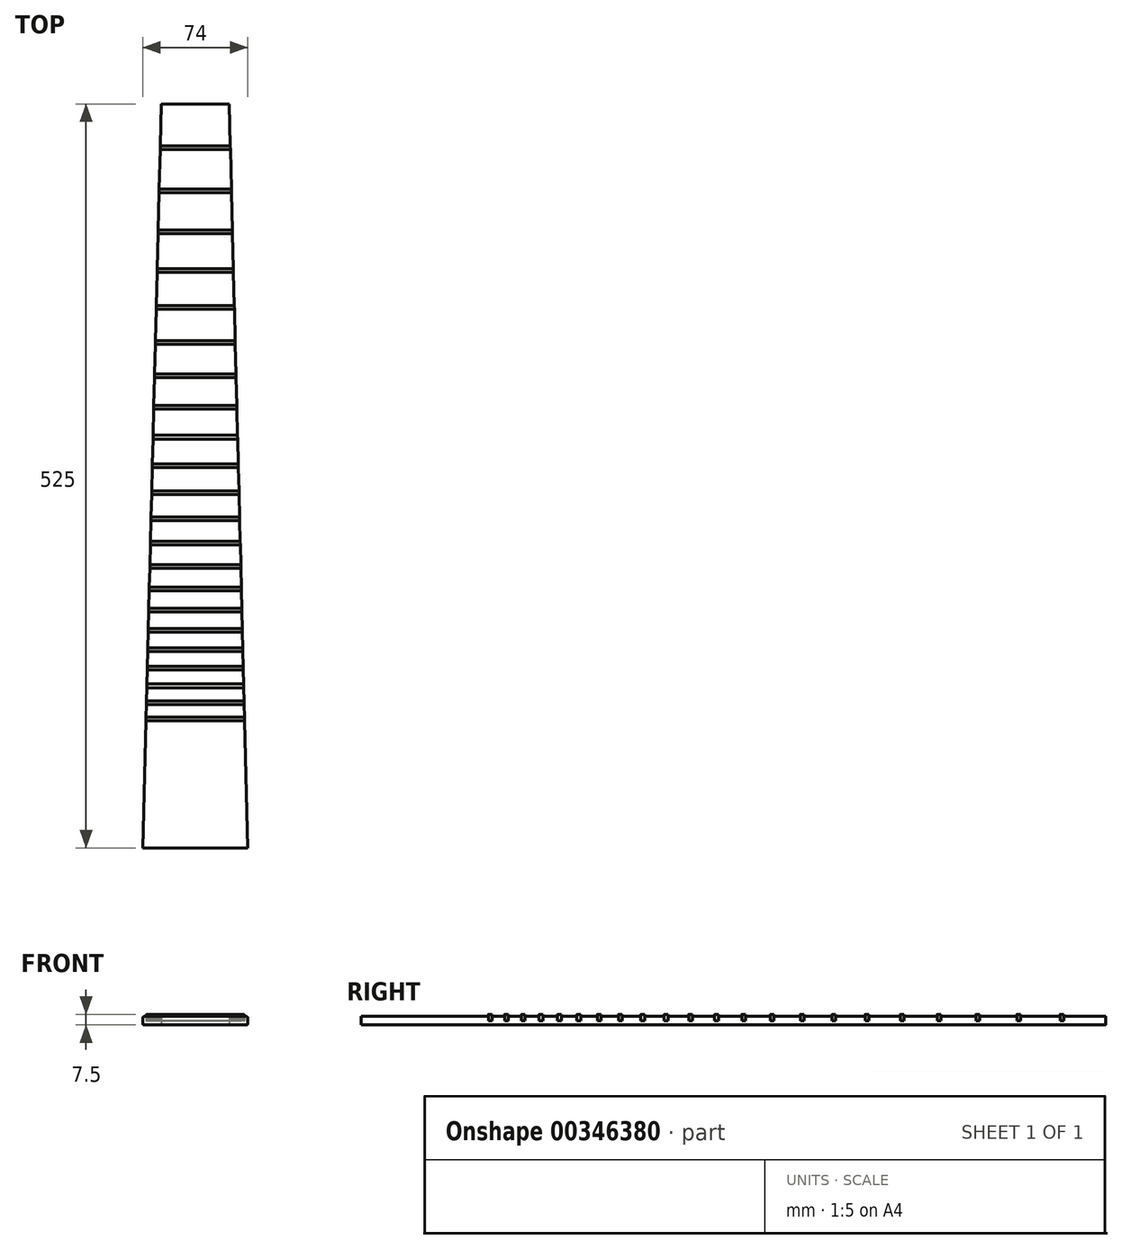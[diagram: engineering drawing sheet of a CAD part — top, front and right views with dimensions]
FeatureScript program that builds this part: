
annotation { "Feature Type Name" : "Feature", "Feature Type Description" : "" }
export const myFeature = defineFeature(function(context is Context, id is Id, definition is map)
    precondition{}
    {
        {
            var Q0;
            Q0=qCreatedBy(makeId("Top.planeOp"),FACE);
            var sketch = newSketch(context, id + "F0", { "sketchPlane" : qUnion([Q0])});
            skLineSegment(sketch, "E0", {"start": v(0, 0) * mm, "end": v(0, 525) * mm, "construction": true});
            skLineSegment(sketch, "E1", {"start": v(0, 525) * mm, "end": v(-24, 525) * mm});
            skLineSegment(sketch, "E2", {"start": v(0, 0) * mm, "end": v(-37, 0) * mm});
            skLineSegment(sketch, "E3", {"start": v(-37, 0) * mm, "end": v(-24, 525) * mm});
            skLineSegment(sketch, "E4", {"start": v(-24.73, 495.53) * mm, "end": v(0, 495.53) * mm});
            skLineSegment(sketch, "E5", {"start": v(-24.8, 492.92) * mm, "end": v(0, 492.92) * mm});
            skLineSegment(sketch, "E6", {"start": v(-25.48, 465.1) * mm, "end": v(0, 465.1) * mm});
            skLineSegment(sketch, "E7", {"start": v(-25.55, 462.49) * mm, "end": v(0, 462.49) * mm});
            skLineSegment(sketch, "E8", {"start": v(-26.2, 436.24) * mm, "end": v(0, 436.24) * mm});
            skLineSegment(sketch, "E9", {"start": v(-26.26, 433.62) * mm, "end": v(0, 433.62) * mm});
            skLineSegment(sketch, "E10", {"start": v(-26.88, 408.84) * mm, "end": v(0, 408.84) * mm});
            skLineSegment(sketch, "E11", {"start": v(-26.94, 406.23) * mm, "end": v(0, 406.23) * mm});
            skLineSegment(sketch, "E12", {"start": v(-27.52, 382.84) * mm, "end": v(0, 382.84) * mm});
            skLineSegment(sketch, "E13", {"start": v(-27.58, 380.22) * mm, "end": v(0, 380.22) * mm});
            skLineSegment(sketch, "E14", {"start": v(-28.13, 358.15) * mm, "end": v(0, 358.15) * mm});
            skLineSegment(sketch, "E15", {"start": v(-28.2, 355.53) * mm, "end": v(0, 355.53) * mm});
            skLineSegment(sketch, "E16", {"start": v(-28.71, 334.7) * mm, "end": v(0, 334.7) * mm});
            skLineSegment(sketch, "E17", {"start": v(-28.78, 332.08) * mm, "end": v(0, 332.08) * mm});
            skLineSegment(sketch, "E18", {"start": v(-29.26, 312.42) * mm, "end": v(0, 312.42) * mm});
            skLineSegment(sketch, "E19", {"start": v(-29.33, 309.8) * mm, "end": v(0, 309.8) * mm});
            skLineSegment(sketch, "E20", {"start": v(-29.79, 291.24) * mm, "end": v(0, 291.24) * mm});
            skLineSegment(sketch, "E21", {"start": v(-29.85, 288.62) * mm, "end": v(0, 288.62) * mm});
            skLineSegment(sketch, "E22", {"start": v(-30.29, 271.1) * mm, "end": v(0, 271.1) * mm});
            skLineSegment(sketch, "E23", {"start": v(-30.35, 268.48) * mm, "end": v(0, 268.48) * mm});
            skLineSegment(sketch, "E24", {"start": v(-30.76, 251.95) * mm, "end": v(0, 251.95) * mm});
            skLineSegment(sketch, "E25", {"start": v(-30.83, 249.33) * mm, "end": v(0, 249.33) * mm});
            skLineSegment(sketch, "E26", {"start": v(-31.21, 233.72) * mm, "end": v(0, 233.72) * mm});
            skLineSegment(sketch, "E27", {"start": v(-31.28, 231.1) * mm, "end": v(0, 231.1) * mm});
            skLineSegment(sketch, "E28", {"start": v(-31.64, 216.37) * mm, "end": v(0, 216.37) * mm});
            skLineSegment(sketch, "E29", {"start": v(-31.7, 213.76) * mm, "end": v(0, 213.76) * mm});
            skLineSegment(sketch, "E30", {"start": v(-32.05, 199.85) * mm, "end": v(0, 199.85) * mm});
            skLineSegment(sketch, "E31", {"start": v(-32.12, 197.23) * mm, "end": v(0, 197.23) * mm});
            skLineSegment(sketch, "E32", {"start": v(-32.44, 184.1) * mm, "end": v(0, 184.1) * mm});
            skLineSegment(sketch, "E33", {"start": v(-32.5, 181.5) * mm, "end": v(0, 181.5) * mm});
            skLineSegment(sketch, "E34", {"start": v(-32.81, 169.1) * mm, "end": v(0, 169.1) * mm});
            skLineSegment(sketch, "E35", {"start": v(-32.88, 166.49) * mm, "end": v(0, 166.49) * mm});
            skLineSegment(sketch, "E36", {"start": v(-33.17, 154.8) * mm, "end": v(0, 154.8) * mm});
            skLineSegment(sketch, "E37", {"start": v(-33.23, 152.18) * mm, "end": v(0, 152.18) * mm});
            skLineSegment(sketch, "E38", {"start": v(-33.5, 141.14) * mm, "end": v(0, 141.14) * mm});
            skLineSegment(sketch, "E39", {"start": v(-33.57, 138.53) * mm, "end": v(0, 138.53) * mm});
            skLineSegment(sketch, "E40", {"start": v(-33.83, 128.1) * mm, "end": v(0, 128.1) * mm});
            skLineSegment(sketch, "E41", {"start": v(-33.9, 125.5) * mm, "end": v(0, 125.5) * mm});
            skLineSegment(sketch, "E42", {"start": v(-34.14, 115.66) * mm, "end": v(0, 115.66) * mm});
            skLineSegment(sketch, "E43", {"start": v(-34.2, 113.04) * mm, "end": v(0, 113.04) * mm});
            skLineSegment(sketch, "E44", {"start": v(-34.43, 103.76) * mm, "end": v(0, 103.76) * mm});
            skLineSegment(sketch, "E45", {"start": v(-34.5, 101.14) * mm, "end": v(0, 101.14) * mm});
            skLineSegment(sketch, "E46", {"start": v(-34.71, 92.38) * mm, "end": v(0, 92.38) * mm});
            skLineSegment(sketch, "E47", {"start": v(-34.78, 89.77) * mm, "end": v(0, 89.77) * mm});
            skLineSegment(sketch, "E48.MirrorCS", {"start": v(0, 525) * mm, "end": v(24, 525) * mm});
            skLineSegment(sketch, "E49.MirrorCS", {"start": v(37, 0) * mm, "end": v(24, 525) * mm});
            skLineSegment(sketch, "E50.MirrorCS", {"start": v(24.73, 495.53) * mm, "end": v(0, 495.53) * mm});
            skLineSegment(sketch, "E51.MirrorCS", {"start": v(24.8, 492.92) * mm, "end": v(0, 492.92) * mm});
            skLineSegment(sketch, "E52.MirrorCS", {"start": v(25.48, 465.1) * mm, "end": v(0, 465.1) * mm});
            skLineSegment(sketch, "E53.MirrorCS", {"start": v(25.55, 462.49) * mm, "end": v(0, 462.49) * mm});
            skLineSegment(sketch, "E54.MirrorCS", {"start": v(26.2, 436.24) * mm, "end": v(0, 436.24) * mm});
            skLineSegment(sketch, "E55.MirrorCS", {"start": v(26.26, 433.62) * mm, "end": v(0, 433.62) * mm});
            skLineSegment(sketch, "E56.MirrorCS", {"start": v(26.88, 408.84) * mm, "end": v(0, 408.84) * mm});
            skLineSegment(sketch, "E57.MirrorCS", {"start": v(26.94, 406.23) * mm, "end": v(0, 406.23) * mm});
            skLineSegment(sketch, "E58.MirrorCS", {"start": v(27.52, 382.84) * mm, "end": v(0, 382.84) * mm});
            skLineSegment(sketch, "E59.MirrorCS", {"start": v(27.58, 380.22) * mm, "end": v(0, 380.22) * mm});
            skLineSegment(sketch, "E60.MirrorCS", {"start": v(28.13, 358.15) * mm, "end": v(0, 358.15) * mm});
            skLineSegment(sketch, "E61.MirrorCS", {"start": v(28.2, 355.53) * mm, "end": v(0, 355.53) * mm});
            skLineSegment(sketch, "E62.MirrorCS", {"start": v(28.71, 334.7) * mm, "end": v(0, 334.7) * mm});
            skLineSegment(sketch, "E63.MirrorCS", {"start": v(28.78, 332.08) * mm, "end": v(0, 332.08) * mm});
            skLineSegment(sketch, "E64.MirrorCS", {"start": v(29.26, 312.42) * mm, "end": v(0, 312.42) * mm});
            skLineSegment(sketch, "E65.MirrorCS", {"start": v(29.33, 309.8) * mm, "end": v(0, 309.8) * mm});
            skLineSegment(sketch, "E66.MirrorCS", {"start": v(29.79, 291.24) * mm, "end": v(0, 291.24) * mm});
            skLineSegment(sketch, "E67.MirrorCS", {"start": v(29.85, 288.62) * mm, "end": v(0, 288.62) * mm});
            skLineSegment(sketch, "E68.MirrorCS", {"start": v(30.29, 271.1) * mm, "end": v(0, 271.1) * mm});
            skLineSegment(sketch, "E69.MirrorCS", {"start": v(30.35, 268.48) * mm, "end": v(0, 268.48) * mm});
            skLineSegment(sketch, "E70.MirrorCS", {"start": v(30.76, 251.95) * mm, "end": v(0, 251.95) * mm});
            skLineSegment(sketch, "E71.MirrorCS", {"start": v(30.83, 249.33) * mm, "end": v(0, 249.33) * mm});
            skLineSegment(sketch, "E72.MirrorCS", {"start": v(31.21, 233.72) * mm, "end": v(0, 233.72) * mm});
            skLineSegment(sketch, "E73.MirrorCS", {"start": v(31.28, 231.1) * mm, "end": v(0, 231.1) * mm});
            skLineSegment(sketch, "E74.MirrorCS", {"start": v(31.64, 216.37) * mm, "end": v(0, 216.37) * mm});
            skLineSegment(sketch, "E75.MirrorCS", {"start": v(31.7, 213.76) * mm, "end": v(0, 213.76) * mm});
            skLineSegment(sketch, "E76.MirrorCS", {"start": v(32.05, 199.85) * mm, "end": v(0, 199.85) * mm});
            skLineSegment(sketch, "E77.MirrorCS", {"start": v(32.12, 197.23) * mm, "end": v(0, 197.23) * mm});
            skLineSegment(sketch, "E78.MirrorCS", {"start": v(32.44, 184.1) * mm, "end": v(0, 184.1) * mm});
            skLineSegment(sketch, "E79.MirrorCS", {"start": v(32.5, 181.5) * mm, "end": v(0, 181.5) * mm});
            skLineSegment(sketch, "E80.MirrorCS", {"start": v(32.81, 169.1) * mm, "end": v(0, 169.1) * mm});
            skLineSegment(sketch, "E81.MirrorCS", {"start": v(32.88, 166.49) * mm, "end": v(0, 166.49) * mm});
            skLineSegment(sketch, "E82.MirrorCS", {"start": v(33.17, 154.8) * mm, "end": v(0, 154.8) * mm});
            skLineSegment(sketch, "E83.MirrorCS", {"start": v(33.23, 152.18) * mm, "end": v(0, 152.18) * mm});
            skLineSegment(sketch, "E84.MirrorCS", {"start": v(33.5, 141.14) * mm, "end": v(0, 141.14) * mm});
            skLineSegment(sketch, "E85.MirrorCS", {"start": v(33.57, 138.53) * mm, "end": v(0, 138.53) * mm});
            skLineSegment(sketch, "E86.MirrorCS", {"start": v(33.83, 128.1) * mm, "end": v(0, 128.1) * mm});
            skLineSegment(sketch, "E87.MirrorCS", {"start": v(33.9, 125.5) * mm, "end": v(0, 125.5) * mm});
            skLineSegment(sketch, "E88.MirrorCS", {"start": v(34.14, 115.66) * mm, "end": v(0, 115.66) * mm});
            skLineSegment(sketch, "E89.MirrorCS", {"start": v(34.2, 113.04) * mm, "end": v(0, 113.04) * mm});
            skLineSegment(sketch, "E90.MirrorCS", {"start": v(34.43, 103.76) * mm, "end": v(0, 103.76) * mm});
            skLineSegment(sketch, "E91.MirrorCS", {"start": v(34.5, 101.14) * mm, "end": v(0, 101.14) * mm});
            skLineSegment(sketch, "E92.MirrorCS", {"start": v(0, 0) * mm, "end": v(37, 0) * mm});
            skLineSegment(sketch, "E93.MirrorCS", {"start": v(34.71, 92.38) * mm, "end": v(0, 92.38) * mm});
            skLineSegment(sketch, "E94.MirrorCS", {"start": v(34.78, 89.77) * mm, "end": v(0, 89.77) * mm});
            skSolve(sketch);
        }
        {
            var Q0;
            Q0=qSketchRegion(id+"F0",true);
            extrude(context, id + "F1", {"entities" : qUnion([Q0]), "endBound" : BoundingType.SYMMETRIC, "depth" : 6 * mm});
        }
        {
            var Q0;
            Q0=makeQuery(id+"F1.opExtrude","CAP_EDGE",EDGE,{"disambiguationData":[OSD([sQuery(id+"F0.wireOp",EDGE,"E3")])],"isStart":true});
            var Q1;
            Q1=makeQuery(id+"F1.opExtrude","CAP_EDGE",EDGE,{"disambiguationData":[OSD([sQuery(id+"F0.wireOp",EDGE,"E49.MirrorCS")])],"isStart":true});
            var Q2;
            Q2=makeQuery(id+"F1.opExtrude","CAP_EDGE",EDGE,{"disambiguationData":[OSD([sQuery(id+"F0.wireOp",EDGE,"E49.MirrorCS")])],"isStart":false});
            var Q3;
            Q3=makeQuery(id+"F1.opExtrude","CAP_EDGE",EDGE,{"disambiguationData":[OSD([sQuery(id+"F0.wireOp",EDGE,"E3")])],"isStart":false});
            fillet(context, id + "F2", {"entities" : qUnion([Q0, Q1, Q2, Q3]), "radius" : 1 * mm, "tangentPropagation" : true, "allowEdgeOverflow" : false});
        }
        {
            var Q0;
            {var subQ1=sQuery(id+"F0.wireOp",EDGE,"E4");Q0=makeQuery(id+"F0.imprint","IMPRINT",FACE,{"disambiguationData":[TD([[makeQuery(id+"F0.imprint","IMPRINT",EDGE,{"derivedFrom":subQ1}),-1.0]])]});}
            var Q1;
            {var subQ1=sQuery(id+"F0.wireOp",EDGE,"E6");Q1=makeQuery(id+"F0.imprint","IMPRINT",FACE,{"disambiguationData":[TD([[makeQuery(id+"F0.imprint","IMPRINT",EDGE,{"derivedFrom":subQ1}),-1.0]])]});}
            var Q2;
            {var subQ1=sQuery(id+"F0.wireOp",EDGE,"E8");Q2=makeQuery(id+"F0.imprint","IMPRINT",FACE,{"disambiguationData":[TD([[makeQuery(id+"F0.imprint","IMPRINT",EDGE,{"derivedFrom":subQ1}),-1.0]])]});}
            var Q3;
            {var subQ0=sQuery(id+"F0.wireOp",EDGE,"E10");Q3=makeQuery(id+"F0.imprint","IMPRINT",FACE,{"disambiguationData":[TD([[makeQuery(id+"F0.imprint","IMPRINT",EDGE,{"derivedFrom":subQ0}),-1.0]])]});}
            var Q4;
            {var subQ1=sQuery(id+"F0.wireOp",EDGE,"E12");Q4=makeQuery(id+"F0.imprint","IMPRINT",FACE,{"disambiguationData":[TD([[makeQuery(id+"F0.imprint","IMPRINT",EDGE,{"derivedFrom":subQ1}),-1.0]])]});}
            var Q5;
            {var subQ1=sQuery(id+"F0.wireOp",EDGE,"E14");Q5=makeQuery(id+"F0.imprint","IMPRINT",FACE,{"disambiguationData":[TD([[makeQuery(id+"F0.imprint","IMPRINT",EDGE,{"derivedFrom":subQ1}),-1.0]])]});}
            var Q6;
            {var subQ1=sQuery(id+"F0.wireOp",EDGE,"E16");Q6=makeQuery(id+"F0.imprint","IMPRINT",FACE,{"disambiguationData":[TD([[makeQuery(id+"F0.imprint","IMPRINT",EDGE,{"derivedFrom":subQ1}),-1.0]])]});}
            var Q7;
            {var subQ4=sQuery(id+"F0.wireOp",EDGE,"E18");Q7=makeQuery(id+"F0.imprint","IMPRINT",FACE,{"disambiguationData":[TD([[makeQuery(id+"F0.imprint","IMPRINT",EDGE,{"derivedFrom":subQ4}),-1.0]])]});}
            var Q8;
            {var subQ0=sQuery(id+"F0.wireOp",EDGE,"E20");Q8=makeQuery(id+"F0.imprint","IMPRINT",FACE,{"disambiguationData":[TD([[makeQuery(id+"F0.imprint","IMPRINT",EDGE,{"derivedFrom":subQ0}),-1.0]])]});}
            var Q9;
            {var subQ1=sQuery(id+"F0.wireOp",EDGE,"E22");Q9=makeQuery(id+"F0.imprint","IMPRINT",FACE,{"disambiguationData":[TD([[makeQuery(id+"F0.imprint","IMPRINT",EDGE,{"derivedFrom":subQ1}),-1.0]])]});}
            var Q10;
            {var subQ1=sQuery(id+"F0.wireOp",EDGE,"E24");Q10=makeQuery(id+"F0.imprint","IMPRINT",FACE,{"disambiguationData":[TD([[makeQuery(id+"F0.imprint","IMPRINT",EDGE,{"derivedFrom":subQ1}),-1.0]])]});}
            var Q11;
            {var subQ1=sQuery(id+"F0.wireOp",EDGE,"E26");Q11=makeQuery(id+"F0.imprint","IMPRINT",FACE,{"disambiguationData":[TD([[makeQuery(id+"F0.imprint","IMPRINT",EDGE,{"derivedFrom":subQ1}),-1.0]])]});}
            var Q12;
            {var subQ4=sQuery(id+"F0.wireOp",EDGE,"E28");Q12=makeQuery(id+"F0.imprint","IMPRINT",FACE,{"disambiguationData":[TD([[makeQuery(id+"F0.imprint","IMPRINT",EDGE,{"derivedFrom":subQ4}),-1.0]])]});}
            var Q13;
            {var subQ0=sQuery(id+"F0.wireOp",EDGE,"E30");Q13=makeQuery(id+"F0.imprint","IMPRINT",FACE,{"disambiguationData":[TD([[makeQuery(id+"F0.imprint","IMPRINT",EDGE,{"derivedFrom":subQ0}),-1.0]])]});}
            var Q14;
            {var subQ1=sQuery(id+"F0.wireOp",EDGE,"E32");Q14=makeQuery(id+"F0.imprint","IMPRINT",FACE,{"disambiguationData":[TD([[makeQuery(id+"F0.imprint","IMPRINT",EDGE,{"derivedFrom":subQ1}),-1.0]])]});}
            var Q15;
            {var subQ1=sQuery(id+"F0.wireOp",EDGE,"E34");Q15=makeQuery(id+"F0.imprint","IMPRINT",FACE,{"disambiguationData":[TD([[makeQuery(id+"F0.imprint","IMPRINT",EDGE,{"derivedFrom":subQ1}),-1.0]])]});}
            var Q16;
            {var subQ1=sQuery(id+"F0.wireOp",EDGE,"E36");Q16=makeQuery(id+"F0.imprint","IMPRINT",FACE,{"disambiguationData":[TD([[makeQuery(id+"F0.imprint","IMPRINT",EDGE,{"derivedFrom":subQ1}),-1.0]])]});}
            var Q17;
            {var subQ4=sQuery(id+"F0.wireOp",EDGE,"E38");Q17=makeQuery(id+"F0.imprint","IMPRINT",FACE,{"disambiguationData":[TD([[makeQuery(id+"F0.imprint","IMPRINT",EDGE,{"derivedFrom":subQ4}),-1.0]])]});}
            var Q18;
            {var subQ0=sQuery(id+"F0.wireOp",EDGE,"E40");Q18=makeQuery(id+"F0.imprint","IMPRINT",FACE,{"disambiguationData":[TD([[makeQuery(id+"F0.imprint","IMPRINT",EDGE,{"derivedFrom":subQ0}),-1.0]])]});}
            var Q19;
            {var subQ1=sQuery(id+"F0.wireOp",EDGE,"E46");Q19=makeQuery(id+"F0.imprint","IMPRINT",FACE,{"disambiguationData":[TD([[makeQuery(id+"F0.imprint","IMPRINT",EDGE,{"derivedFrom":subQ1}),-1.0]])]});}
            var Q20;
            {var subQ1=sQuery(id+"F0.wireOp",EDGE,"E44");Q20=makeQuery(id+"F0.imprint","IMPRINT",FACE,{"disambiguationData":[TD([[makeQuery(id+"F0.imprint","IMPRINT",EDGE,{"derivedFrom":subQ1}),-1.0]])]});}
            var Q21;
            {var subQ4=sQuery(id+"F0.wireOp",EDGE,"E42");Q21=makeQuery(id+"F0.imprint","IMPRINT",FACE,{"disambiguationData":[TD([[makeQuery(id+"F0.imprint","IMPRINT",EDGE,{"derivedFrom":subQ4}),-1.0]])]});}
            extrude(context, id + "F3", {"entities" : qUnion([Q0, Q1, Q2, Q3, Q4, Q5, Q6, Q7, Q8, Q9, Q10, Q11, Q12, Q13, Q14, Q15, Q16, Q17, Q18, Q19, Q20, Q21]), "depth" : 4.5 * mm});
        }
        {
            var Q0;
            Q0=makeQuery(id+"F3.opExtrude","SWEPT_BODY",BODY,{"disambiguationData":[OSD([sQuery(id+"F0.wireOp",EDGE,"E3"),sQuery(id+"F0.wireOp",EDGE,"E46"),sQuery(id+"F0.wireOp",EDGE,"E47"),sQuery(id+"F0.wireOp",EDGE,"E49.MirrorCS"),sQuery(id+"F0.wireOp",EDGE,"E93.MirrorCS"),sQuery(id+"F0.wireOp",EDGE,"E94.MirrorCS")])]});
            var Q1;
            Q1=makeQuery(id+"F3.opExtrude","SWEPT_BODY",BODY,{"disambiguationData":[OSD([sQuery(id+"F0.wireOp",EDGE,"E3"),sQuery(id+"F0.wireOp",EDGE,"E44"),sQuery(id+"F0.wireOp",EDGE,"E45"),sQuery(id+"F0.wireOp",EDGE,"E49.MirrorCS"),sQuery(id+"F0.wireOp",EDGE,"E90.MirrorCS"),sQuery(id+"F0.wireOp",EDGE,"E91.MirrorCS")])]});
            var Q2;
            Q2=makeQuery(id+"F3.opExtrude","SWEPT_BODY",BODY,{"disambiguationData":[OSD([sQuery(id+"F0.wireOp",EDGE,"E3"),sQuery(id+"F0.wireOp",EDGE,"E42"),sQuery(id+"F0.wireOp",EDGE,"E43"),sQuery(id+"F0.wireOp",EDGE,"E49.MirrorCS"),sQuery(id+"F0.wireOp",EDGE,"E88.MirrorCS"),sQuery(id+"F0.wireOp",EDGE,"E89.MirrorCS")])]});
            var Q3;
            Q3=makeQuery(id+"F3.opExtrude","SWEPT_BODY",BODY,{"disambiguationData":[OSD([sQuery(id+"F0.wireOp",EDGE,"E3"),sQuery(id+"F0.wireOp",EDGE,"E40"),sQuery(id+"F0.wireOp",EDGE,"E41"),sQuery(id+"F0.wireOp",EDGE,"E49.MirrorCS"),sQuery(id+"F0.wireOp",EDGE,"E86.MirrorCS"),sQuery(id+"F0.wireOp",EDGE,"E87.MirrorCS")])]});
            var Q4;
            Q4=makeQuery(id+"F3.opExtrude","SWEPT_BODY",BODY,{"disambiguationData":[OSD([sQuery(id+"F0.wireOp",EDGE,"E3"),sQuery(id+"F0.wireOp",EDGE,"E38"),sQuery(id+"F0.wireOp",EDGE,"E39"),sQuery(id+"F0.wireOp",EDGE,"E49.MirrorCS"),sQuery(id+"F0.wireOp",EDGE,"E84.MirrorCS"),sQuery(id+"F0.wireOp",EDGE,"E85.MirrorCS")])]});
            var Q5;
            Q5=makeQuery(id+"F3.opExtrude","SWEPT_BODY",BODY,{"disambiguationData":[OSD([sQuery(id+"F0.wireOp",EDGE,"E3"),sQuery(id+"F0.wireOp",EDGE,"E36"),sQuery(id+"F0.wireOp",EDGE,"E37"),sQuery(id+"F0.wireOp",EDGE,"E49.MirrorCS"),sQuery(id+"F0.wireOp",EDGE,"E82.MirrorCS"),sQuery(id+"F0.wireOp",EDGE,"E83.MirrorCS")])]});
            var Q6;
            Q6=makeQuery(id+"F3.opExtrude","SWEPT_BODY",BODY,{"disambiguationData":[OSD([sQuery(id+"F0.wireOp",EDGE,"E3"),sQuery(id+"F0.wireOp",EDGE,"E34"),sQuery(id+"F0.wireOp",EDGE,"E35"),sQuery(id+"F0.wireOp",EDGE,"E49.MirrorCS"),sQuery(id+"F0.wireOp",EDGE,"E80.MirrorCS"),sQuery(id+"F0.wireOp",EDGE,"E81.MirrorCS")])]});
            var Q7;
            Q7=makeQuery(id+"F3.opExtrude","SWEPT_BODY",BODY,{"disambiguationData":[OSD([sQuery(id+"F0.wireOp",EDGE,"E3"),sQuery(id+"F0.wireOp",EDGE,"E32"),sQuery(id+"F0.wireOp",EDGE,"E33"),sQuery(id+"F0.wireOp",EDGE,"E49.MirrorCS"),sQuery(id+"F0.wireOp",EDGE,"E78.MirrorCS"),sQuery(id+"F0.wireOp",EDGE,"E79.MirrorCS")])]});
            var Q8;
            Q8=makeQuery(id+"F3.opExtrude","SWEPT_BODY",BODY,{"disambiguationData":[OSD([sQuery(id+"F0.wireOp",EDGE,"E3"),sQuery(id+"F0.wireOp",EDGE,"E30"),sQuery(id+"F0.wireOp",EDGE,"E31"),sQuery(id+"F0.wireOp",EDGE,"E49.MirrorCS"),sQuery(id+"F0.wireOp",EDGE,"E76.MirrorCS"),sQuery(id+"F0.wireOp",EDGE,"E77.MirrorCS")])]});
            var Q9;
            Q9=makeQuery(id+"F3.opExtrude","SWEPT_BODY",BODY,{"disambiguationData":[OSD([sQuery(id+"F0.wireOp",EDGE,"E3"),sQuery(id+"F0.wireOp",EDGE,"E28"),sQuery(id+"F0.wireOp",EDGE,"E29"),sQuery(id+"F0.wireOp",EDGE,"E49.MirrorCS"),sQuery(id+"F0.wireOp",EDGE,"E74.MirrorCS"),sQuery(id+"F0.wireOp",EDGE,"E75.MirrorCS")])]});
            var Q10;
            Q10=makeQuery(id+"F3.opExtrude","SWEPT_BODY",BODY,{"disambiguationData":[OSD([sQuery(id+"F0.wireOp",EDGE,"E3"),sQuery(id+"F0.wireOp",EDGE,"E26"),sQuery(id+"F0.wireOp",EDGE,"E27"),sQuery(id+"F0.wireOp",EDGE,"E49.MirrorCS"),sQuery(id+"F0.wireOp",EDGE,"E72.MirrorCS"),sQuery(id+"F0.wireOp",EDGE,"E73.MirrorCS")])]});
            var Q11;
            Q11=makeQuery(id+"F3.opExtrude","SWEPT_BODY",BODY,{"disambiguationData":[OSD([sQuery(id+"F0.wireOp",EDGE,"E3"),sQuery(id+"F0.wireOp",EDGE,"E24"),sQuery(id+"F0.wireOp",EDGE,"E25"),sQuery(id+"F0.wireOp",EDGE,"E49.MirrorCS"),sQuery(id+"F0.wireOp",EDGE,"E70.MirrorCS"),sQuery(id+"F0.wireOp",EDGE,"E71.MirrorCS")])]});
            var Q12;
            Q12=makeQuery(id+"F3.opExtrude","SWEPT_BODY",BODY,{"disambiguationData":[OSD([sQuery(id+"F0.wireOp",EDGE,"E3"),sQuery(id+"F0.wireOp",EDGE,"E22"),sQuery(id+"F0.wireOp",EDGE,"E23"),sQuery(id+"F0.wireOp",EDGE,"E49.MirrorCS"),sQuery(id+"F0.wireOp",EDGE,"E68.MirrorCS"),sQuery(id+"F0.wireOp",EDGE,"E69.MirrorCS")])]});
            var Q13;
            Q13=makeQuery(id+"F3.opExtrude","SWEPT_BODY",BODY,{"disambiguationData":[OSD([sQuery(id+"F0.wireOp",EDGE,"E3"),sQuery(id+"F0.wireOp",EDGE,"E20"),sQuery(id+"F0.wireOp",EDGE,"E21"),sQuery(id+"F0.wireOp",EDGE,"E49.MirrorCS"),sQuery(id+"F0.wireOp",EDGE,"E66.MirrorCS"),sQuery(id+"F0.wireOp",EDGE,"E67.MirrorCS")])]});
            var Q14;
            Q14=makeQuery(id+"F3.opExtrude","SWEPT_BODY",BODY,{"disambiguationData":[OSD([sQuery(id+"F0.wireOp",EDGE,"E3"),sQuery(id+"F0.wireOp",EDGE,"E18"),sQuery(id+"F0.wireOp",EDGE,"E19"),sQuery(id+"F0.wireOp",EDGE,"E49.MirrorCS"),sQuery(id+"F0.wireOp",EDGE,"E64.MirrorCS"),sQuery(id+"F0.wireOp",EDGE,"E65.MirrorCS")])]});
            var Q15;
            Q15=makeQuery(id+"F3.opExtrude","SWEPT_BODY",BODY,{"disambiguationData":[OSD([sQuery(id+"F0.wireOp",EDGE,"E3"),sQuery(id+"F0.wireOp",EDGE,"E16"),sQuery(id+"F0.wireOp",EDGE,"E17"),sQuery(id+"F0.wireOp",EDGE,"E49.MirrorCS"),sQuery(id+"F0.wireOp",EDGE,"E62.MirrorCS"),sQuery(id+"F0.wireOp",EDGE,"E63.MirrorCS")])]});
            var Q16;
            Q16=makeQuery(id+"F3.opExtrude","SWEPT_BODY",BODY,{"disambiguationData":[OSD([sQuery(id+"F0.wireOp",EDGE,"E3"),sQuery(id+"F0.wireOp",EDGE,"E14"),sQuery(id+"F0.wireOp",EDGE,"E15"),sQuery(id+"F0.wireOp",EDGE,"E49.MirrorCS"),sQuery(id+"F0.wireOp",EDGE,"E60.MirrorCS"),sQuery(id+"F0.wireOp",EDGE,"E61.MirrorCS")])]});
            var Q17;
            Q17=makeQuery(id+"F3.opExtrude","SWEPT_BODY",BODY,{"disambiguationData":[OSD([sQuery(id+"F0.wireOp",EDGE,"E3"),sQuery(id+"F0.wireOp",EDGE,"E12"),sQuery(id+"F0.wireOp",EDGE,"E13"),sQuery(id+"F0.wireOp",EDGE,"E49.MirrorCS"),sQuery(id+"F0.wireOp",EDGE,"E58.MirrorCS"),sQuery(id+"F0.wireOp",EDGE,"E59.MirrorCS")])]});
            var Q18;
            Q18=makeQuery(id+"F3.opExtrude","SWEPT_BODY",BODY,{"disambiguationData":[OSD([sQuery(id+"F0.wireOp",EDGE,"E3"),sQuery(id+"F0.wireOp",EDGE,"E10"),sQuery(id+"F0.wireOp",EDGE,"E11"),sQuery(id+"F0.wireOp",EDGE,"E49.MirrorCS"),sQuery(id+"F0.wireOp",EDGE,"E56.MirrorCS"),sQuery(id+"F0.wireOp",EDGE,"E57.MirrorCS")])]});
            var Q19;
            Q19=makeQuery(id+"F3.opExtrude","SWEPT_BODY",BODY,{"disambiguationData":[OSD([sQuery(id+"F0.wireOp",EDGE,"E3"),sQuery(id+"F0.wireOp",EDGE,"E8"),sQuery(id+"F0.wireOp",EDGE,"E9"),sQuery(id+"F0.wireOp",EDGE,"E49.MirrorCS"),sQuery(id+"F0.wireOp",EDGE,"E54.MirrorCS"),sQuery(id+"F0.wireOp",EDGE,"E55.MirrorCS")])]});
            var Q20;
            Q20=makeQuery(id+"F3.opExtrude","SWEPT_BODY",BODY,{"disambiguationData":[OSD([sQuery(id+"F0.wireOp",EDGE,"E3"),sQuery(id+"F0.wireOp",EDGE,"E6"),sQuery(id+"F0.wireOp",EDGE,"E7"),sQuery(id+"F0.wireOp",EDGE,"E49.MirrorCS"),sQuery(id+"F0.wireOp",EDGE,"E52.MirrorCS"),sQuery(id+"F0.wireOp",EDGE,"E53.MirrorCS")])]});
            var Q21;
            Q21=makeQuery(id+"F3.opExtrude","SWEPT_BODY",BODY,{"disambiguationData":[OSD([sQuery(id+"F0.wireOp",EDGE,"E3"),sQuery(id+"F0.wireOp",EDGE,"E4"),sQuery(id+"F0.wireOp",EDGE,"E5"),sQuery(id+"F0.wireOp",EDGE,"E49.MirrorCS"),sQuery(id+"F0.wireOp",EDGE,"E50.MirrorCS"),sQuery(id+"F0.wireOp",EDGE,"E51.MirrorCS")])]});
            var Q22;
            Q22=makeQuery(id+"F1.opExtrude","SWEPT_BODY",BODY,{"disambiguationData":[OSD([sQuery(id+"F0.wireOp",EDGE,"E1"),sQuery(id+"F0.wireOp",EDGE,"E2"),sQuery(id+"F0.wireOp",EDGE,"E3"),sQuery(id+"F0.wireOp",EDGE,"E48.MirrorCS"),sQuery(id+"F0.wireOp",EDGE,"E49.MirrorCS"),sQuery(id+"F0.wireOp",EDGE,"E92.MirrorCS")])]});
            booleanBodies(context, id + "F4", {"operationType" : BooleanOperationType.SUBTRACTION, "tools" : qUnion([Q0, Q1, Q2, Q3, Q4, Q5, Q6, Q7, Q8, Q9, Q10, Q11, Q12, Q13, Q14, Q15, Q16, Q17, Q18, Q19, Q20, Q21]), "targets" : qUnion([Q22]), "keepTools" : true});
        }
        {
            var Q0;
            {var subQ0=sQuery(id+"F0.wireOp",EDGE,"E3");Q0=makeQuery(id+"F3.opExtrude","CAP_EDGE",EDGE,{"disambiguationData":[OSD([subQ0]),TDD([makeQuery(id+"F0.imprint","IMPRINT",EDGE,{"disambiguationData":[TD([[makeQuery(id+"F0.imprint","INTERSECT",VERTEX,{"derivedFrom":[subQ0,sQuery(id+"F0.wireOp",EDGE,"E4")]}),1.0]])],"derivedFrom":subQ0})])],"isStart":false});}
            var Q1;
            {var subQ0=sQuery(id+"F0.wireOp",EDGE,"E49.MirrorCS");Q1=makeQuery(id+"F3.opExtrude","CAP_EDGE",EDGE,{"disambiguationData":[OSD([subQ0]),TDD([makeQuery(id+"F0.imprint","IMPRINT",EDGE,{"disambiguationData":[TD([[makeQuery(id+"F0.imprint","INTERSECT",VERTEX,{"derivedFrom":[subQ0,sQuery(id+"F0.wireOp",EDGE,"E50.MirrorCS")]}),1.0]])],"derivedFrom":subQ0})])],"isStart":false});}
            var Q2;
            {var subQ0=sQuery(id+"F0.wireOp",EDGE,"E49.MirrorCS");Q2=makeQuery(id+"F3.opExtrude","CAP_EDGE",EDGE,{"disambiguationData":[OSD([subQ0]),TDD([makeQuery(id+"F0.imprint","IMPRINT",EDGE,{"disambiguationData":[TD([[makeQuery(id+"F0.imprint","INTERSECT",VERTEX,{"derivedFrom":[subQ0,sQuery(id+"F0.wireOp",EDGE,"E52.MirrorCS")]}),1.0]])],"derivedFrom":subQ0})])],"isStart":false});}
            var Q3;
            {var subQ0=sQuery(id+"F0.wireOp",EDGE,"E3");Q3=makeQuery(id+"F3.opExtrude","CAP_EDGE",EDGE,{"disambiguationData":[OSD([subQ0]),TDD([makeQuery(id+"F0.imprint","IMPRINT",EDGE,{"disambiguationData":[TD([[makeQuery(id+"F0.imprint","INTERSECT",VERTEX,{"derivedFrom":[subQ0,sQuery(id+"F0.wireOp",EDGE,"E6")]}),1.0]])],"derivedFrom":subQ0})])],"isStart":false});}
            var Q4;
            {var subQ0=sQuery(id+"F0.wireOp",EDGE,"E3");Q4=makeQuery(id+"F3.opExtrude","CAP_EDGE",EDGE,{"disambiguationData":[OSD([subQ0]),TDD([makeQuery(id+"F0.imprint","IMPRINT",EDGE,{"disambiguationData":[TD([[makeQuery(id+"F0.imprint","INTERSECT",VERTEX,{"derivedFrom":[subQ0,sQuery(id+"F0.wireOp",EDGE,"E8")]}),1.0]])],"derivedFrom":subQ0})])],"isStart":false});}
            var Q5;
            {var subQ0=sQuery(id+"F0.wireOp",EDGE,"E49.MirrorCS");Q5=makeQuery(id+"F3.opExtrude","CAP_EDGE",EDGE,{"disambiguationData":[OSD([subQ0]),TDD([makeQuery(id+"F0.imprint","IMPRINT",EDGE,{"disambiguationData":[TD([[makeQuery(id+"F0.imprint","INTERSECT",VERTEX,{"derivedFrom":[subQ0,sQuery(id+"F0.wireOp",EDGE,"E54.MirrorCS")]}),1.0]])],"derivedFrom":subQ0})])],"isStart":false});}
            var Q6;
            {var subQ0=sQuery(id+"F0.wireOp",EDGE,"E3");Q6=makeQuery(id+"F3.opExtrude","CAP_EDGE",EDGE,{"disambiguationData":[OSD([subQ0]),TDD([makeQuery(id+"F0.imprint","IMPRINT",EDGE,{"disambiguationData":[TD([[makeQuery(id+"F0.imprint","INTERSECT",VERTEX,{"derivedFrom":[subQ0,sQuery(id+"F0.wireOp",EDGE,"E10")]}),1.0]])],"derivedFrom":subQ0})])],"isStart":false});}
            var Q7;
            {var subQ0=sQuery(id+"F0.wireOp",EDGE,"E49.MirrorCS");Q7=makeQuery(id+"F3.opExtrude","CAP_EDGE",EDGE,{"disambiguationData":[OSD([subQ0]),TDD([makeQuery(id+"F0.imprint","IMPRINT",EDGE,{"disambiguationData":[TD([[makeQuery(id+"F0.imprint","INTERSECT",VERTEX,{"derivedFrom":[subQ0,sQuery(id+"F0.wireOp",EDGE,"E56.MirrorCS")]}),1.0]])],"derivedFrom":subQ0})])],"isStart":false});}
            var Q8;
            {var subQ0=sQuery(id+"F0.wireOp",EDGE,"E49.MirrorCS");Q8=makeQuery(id+"F3.opExtrude","CAP_EDGE",EDGE,{"disambiguationData":[OSD([subQ0]),TDD([makeQuery(id+"F0.imprint","IMPRINT",EDGE,{"disambiguationData":[TD([[makeQuery(id+"F0.imprint","INTERSECT",VERTEX,{"derivedFrom":[subQ0,sQuery(id+"F0.wireOp",EDGE,"E58.MirrorCS")]}),1.0]])],"derivedFrom":subQ0})])],"isStart":false});}
            var Q9;
            {var subQ0=sQuery(id+"F0.wireOp",EDGE,"E3");Q9=makeQuery(id+"F3.opExtrude","CAP_EDGE",EDGE,{"disambiguationData":[OSD([subQ0]),TDD([makeQuery(id+"F0.imprint","IMPRINT",EDGE,{"disambiguationData":[TD([[makeQuery(id+"F0.imprint","INTERSECT",VERTEX,{"derivedFrom":[subQ0,sQuery(id+"F0.wireOp",EDGE,"E12")]}),1.0]])],"derivedFrom":subQ0})])],"isStart":false});}
            var Q10;
            {var subQ0=sQuery(id+"F0.wireOp",EDGE,"E3");Q10=makeQuery(id+"F3.opExtrude","CAP_EDGE",EDGE,{"disambiguationData":[OSD([subQ0]),TDD([makeQuery(id+"F0.imprint","IMPRINT",EDGE,{"disambiguationData":[TD([[makeQuery(id+"F0.imprint","INTERSECT",VERTEX,{"derivedFrom":[subQ0,sQuery(id+"F0.wireOp",EDGE,"E14")]}),1.0]])],"derivedFrom":subQ0})])],"isStart":false});}
            var Q11;
            {var subQ0=sQuery(id+"F0.wireOp",EDGE,"E49.MirrorCS");Q11=makeQuery(id+"F3.opExtrude","CAP_EDGE",EDGE,{"disambiguationData":[OSD([subQ0]),TDD([makeQuery(id+"F0.imprint","IMPRINT",EDGE,{"disambiguationData":[TD([[makeQuery(id+"F0.imprint","INTERSECT",VERTEX,{"derivedFrom":[subQ0,sQuery(id+"F0.wireOp",EDGE,"E60.MirrorCS")]}),1.0]])],"derivedFrom":subQ0})])],"isStart":false});}
            var Q12;
            {var subQ0=sQuery(id+"F0.wireOp",EDGE,"E49.MirrorCS");Q12=makeQuery(id+"F3.opExtrude","CAP_EDGE",EDGE,{"disambiguationData":[OSD([subQ0]),TDD([makeQuery(id+"F0.imprint","IMPRINT",EDGE,{"disambiguationData":[TD([[makeQuery(id+"F0.imprint","INTERSECT",VERTEX,{"derivedFrom":[subQ0,sQuery(id+"F0.wireOp",EDGE,"E62.MirrorCS")]}),1.0]])],"derivedFrom":subQ0})])],"isStart":false});}
            var Q13;
            {var subQ0=sQuery(id+"F0.wireOp",EDGE,"E3");Q13=makeQuery(id+"F3.opExtrude","CAP_EDGE",EDGE,{"disambiguationData":[OSD([subQ0]),TDD([makeQuery(id+"F0.imprint","IMPRINT",EDGE,{"disambiguationData":[TD([[makeQuery(id+"F0.imprint","INTERSECT",VERTEX,{"derivedFrom":[subQ0,sQuery(id+"F0.wireOp",EDGE,"E16")]}),1.0]])],"derivedFrom":subQ0})])],"isStart":false});}
            var Q14;
            {var subQ0=sQuery(id+"F0.wireOp",EDGE,"E3");Q14=makeQuery(id+"F3.opExtrude","CAP_EDGE",EDGE,{"disambiguationData":[OSD([subQ0]),TDD([makeQuery(id+"F0.imprint","IMPRINT",EDGE,{"disambiguationData":[TD([[makeQuery(id+"F0.imprint","INTERSECT",VERTEX,{"derivedFrom":[subQ0,sQuery(id+"F0.wireOp",EDGE,"E18")]}),1.0]])],"derivedFrom":subQ0})])],"isStart":false});}
            var Q15;
            {var subQ0=sQuery(id+"F0.wireOp",EDGE,"E49.MirrorCS");Q15=makeQuery(id+"F3.opExtrude","CAP_EDGE",EDGE,{"disambiguationData":[OSD([subQ0]),TDD([makeQuery(id+"F0.imprint","IMPRINT",EDGE,{"disambiguationData":[TD([[makeQuery(id+"F0.imprint","INTERSECT",VERTEX,{"derivedFrom":[subQ0,sQuery(id+"F0.wireOp",EDGE,"E64.MirrorCS")]}),1.0]])],"derivedFrom":subQ0})])],"isStart":false});}
            var Q16;
            {var subQ0=sQuery(id+"F0.wireOp",EDGE,"E49.MirrorCS");Q16=makeQuery(id+"F3.opExtrude","CAP_EDGE",EDGE,{"disambiguationData":[OSD([subQ0]),TDD([makeQuery(id+"F0.imprint","IMPRINT",EDGE,{"disambiguationData":[TD([[makeQuery(id+"F0.imprint","INTERSECT",VERTEX,{"derivedFrom":[subQ0,sQuery(id+"F0.wireOp",EDGE,"E66.MirrorCS")]}),1.0]])],"derivedFrom":subQ0})])],"isStart":false});}
            var Q17;
            {var subQ0=sQuery(id+"F0.wireOp",EDGE,"E3");Q17=makeQuery(id+"F3.opExtrude","CAP_EDGE",EDGE,{"disambiguationData":[OSD([subQ0]),TDD([makeQuery(id+"F0.imprint","IMPRINT",EDGE,{"disambiguationData":[TD([[makeQuery(id+"F0.imprint","INTERSECT",VERTEX,{"derivedFrom":[subQ0,sQuery(id+"F0.wireOp",EDGE,"E20")]}),1.0]])],"derivedFrom":subQ0})])],"isStart":false});}
            var Q18;
            {var subQ0=sQuery(id+"F0.wireOp",EDGE,"E3");Q18=makeQuery(id+"F3.opExtrude","CAP_EDGE",EDGE,{"disambiguationData":[OSD([subQ0]),TDD([makeQuery(id+"F0.imprint","IMPRINT",EDGE,{"disambiguationData":[TD([[makeQuery(id+"F0.imprint","INTERSECT",VERTEX,{"derivedFrom":[subQ0,sQuery(id+"F0.wireOp",EDGE,"E22")]}),1.0]])],"derivedFrom":subQ0})])],"isStart":false});}
            var Q19;
            {var subQ0=sQuery(id+"F0.wireOp",EDGE,"E49.MirrorCS");Q19=makeQuery(id+"F3.opExtrude","CAP_EDGE",EDGE,{"disambiguationData":[OSD([subQ0]),TDD([makeQuery(id+"F0.imprint","IMPRINT",EDGE,{"disambiguationData":[TD([[makeQuery(id+"F0.imprint","INTERSECT",VERTEX,{"derivedFrom":[subQ0,sQuery(id+"F0.wireOp",EDGE,"E68.MirrorCS")]}),1.0]])],"derivedFrom":subQ0})])],"isStart":false});}
            var Q20;
            {var subQ0=sQuery(id+"F0.wireOp",EDGE,"E49.MirrorCS");Q20=makeQuery(id+"F3.opExtrude","CAP_EDGE",EDGE,{"disambiguationData":[OSD([subQ0]),TDD([makeQuery(id+"F0.imprint","IMPRINT",EDGE,{"disambiguationData":[TD([[makeQuery(id+"F0.imprint","INTERSECT",VERTEX,{"derivedFrom":[subQ0,sQuery(id+"F0.wireOp",EDGE,"E70.MirrorCS")]}),1.0]])],"derivedFrom":subQ0})])],"isStart":false});}
            var Q21;
            {var subQ0=sQuery(id+"F0.wireOp",EDGE,"E3");Q21=makeQuery(id+"F3.opExtrude","CAP_EDGE",EDGE,{"disambiguationData":[OSD([subQ0]),TDD([makeQuery(id+"F0.imprint","IMPRINT",EDGE,{"disambiguationData":[TD([[makeQuery(id+"F0.imprint","INTERSECT",VERTEX,{"derivedFrom":[subQ0,sQuery(id+"F0.wireOp",EDGE,"E24")]}),1.0]])],"derivedFrom":subQ0})])],"isStart":false});}
            var Q22;
            {var subQ0=sQuery(id+"F0.wireOp",EDGE,"E3");Q22=makeQuery(id+"F3.opExtrude","CAP_EDGE",EDGE,{"disambiguationData":[OSD([subQ0]),TDD([makeQuery(id+"F0.imprint","IMPRINT",EDGE,{"disambiguationData":[TD([[makeQuery(id+"F0.imprint","INTERSECT",VERTEX,{"derivedFrom":[subQ0,sQuery(id+"F0.wireOp",EDGE,"E26")]}),1.0]])],"derivedFrom":subQ0})])],"isStart":false});}
            var Q23;
            {var subQ0=sQuery(id+"F0.wireOp",EDGE,"E49.MirrorCS");Q23=makeQuery(id+"F3.opExtrude","CAP_EDGE",EDGE,{"disambiguationData":[OSD([subQ0]),TDD([makeQuery(id+"F0.imprint","IMPRINT",EDGE,{"disambiguationData":[TD([[makeQuery(id+"F0.imprint","INTERSECT",VERTEX,{"derivedFrom":[subQ0,sQuery(id+"F0.wireOp",EDGE,"E72.MirrorCS")]}),1.0]])],"derivedFrom":subQ0})])],"isStart":false});}
            var Q24;
            {var subQ0=sQuery(id+"F0.wireOp",EDGE,"E3");Q24=makeQuery(id+"F3.opExtrude","CAP_EDGE",EDGE,{"disambiguationData":[OSD([subQ0]),TDD([makeQuery(id+"F0.imprint","IMPRINT",EDGE,{"disambiguationData":[TD([[makeQuery(id+"F0.imprint","INTERSECT",VERTEX,{"derivedFrom":[subQ0,sQuery(id+"F0.wireOp",EDGE,"E28")]}),1.0]])],"derivedFrom":subQ0})])],"isStart":false});}
            var Q25;
            {var subQ0=sQuery(id+"F0.wireOp",EDGE,"E49.MirrorCS");Q25=makeQuery(id+"F3.opExtrude","CAP_EDGE",EDGE,{"disambiguationData":[OSD([subQ0]),TDD([makeQuery(id+"F0.imprint","IMPRINT",EDGE,{"disambiguationData":[TD([[makeQuery(id+"F0.imprint","INTERSECT",VERTEX,{"derivedFrom":[subQ0,sQuery(id+"F0.wireOp",EDGE,"E74.MirrorCS")]}),1.0]])],"derivedFrom":subQ0})])],"isStart":false});}
            var Q26;
            {var subQ0=sQuery(id+"F0.wireOp",EDGE,"E49.MirrorCS");Q26=makeQuery(id+"F3.opExtrude","CAP_EDGE",EDGE,{"disambiguationData":[OSD([subQ0]),TDD([makeQuery(id+"F0.imprint","IMPRINT",EDGE,{"disambiguationData":[TD([[makeQuery(id+"F0.imprint","INTERSECT",VERTEX,{"derivedFrom":[subQ0,sQuery(id+"F0.wireOp",EDGE,"E76.MirrorCS")]}),1.0]])],"derivedFrom":subQ0})])],"isStart":false});}
            var Q27;
            {var subQ0=sQuery(id+"F0.wireOp",EDGE,"E3");Q27=makeQuery(id+"F3.opExtrude","CAP_EDGE",EDGE,{"disambiguationData":[OSD([subQ0]),TDD([makeQuery(id+"F0.imprint","IMPRINT",EDGE,{"disambiguationData":[TD([[makeQuery(id+"F0.imprint","INTERSECT",VERTEX,{"derivedFrom":[subQ0,sQuery(id+"F0.wireOp",EDGE,"E30")]}),1.0]])],"derivedFrom":subQ0})])],"isStart":false});}
            var Q28;
            {var subQ0=sQuery(id+"F0.wireOp",EDGE,"E3");Q28=makeQuery(id+"F3.opExtrude","CAP_EDGE",EDGE,{"disambiguationData":[OSD([subQ0]),TDD([makeQuery(id+"F0.imprint","IMPRINT",EDGE,{"disambiguationData":[TD([[makeQuery(id+"F0.imprint","INTERSECT",VERTEX,{"derivedFrom":[subQ0,sQuery(id+"F0.wireOp",EDGE,"E32")]}),1.0]])],"derivedFrom":subQ0})])],"isStart":false});}
            var Q29;
            {var subQ0=sQuery(id+"F0.wireOp",EDGE,"E49.MirrorCS");Q29=makeQuery(id+"F3.opExtrude","CAP_EDGE",EDGE,{"disambiguationData":[OSD([subQ0]),TDD([makeQuery(id+"F0.imprint","IMPRINT",EDGE,{"disambiguationData":[TD([[makeQuery(id+"F0.imprint","INTERSECT",VERTEX,{"derivedFrom":[subQ0,sQuery(id+"F0.wireOp",EDGE,"E78.MirrorCS")]}),1.0]])],"derivedFrom":subQ0})])],"isStart":false});}
            var Q30;
            {var subQ0=sQuery(id+"F0.wireOp",EDGE,"E49.MirrorCS");Q30=makeQuery(id+"F3.opExtrude","CAP_EDGE",EDGE,{"disambiguationData":[OSD([subQ0]),TDD([makeQuery(id+"F0.imprint","IMPRINT",EDGE,{"disambiguationData":[TD([[makeQuery(id+"F0.imprint","INTERSECT",VERTEX,{"derivedFrom":[subQ0,sQuery(id+"F0.wireOp",EDGE,"E80.MirrorCS")]}),1.0]])],"derivedFrom":subQ0})])],"isStart":false});}
            var Q31;
            {var subQ0=sQuery(id+"F0.wireOp",EDGE,"E3");Q31=makeQuery(id+"F3.opExtrude","CAP_EDGE",EDGE,{"disambiguationData":[OSD([subQ0]),TDD([makeQuery(id+"F0.imprint","IMPRINT",EDGE,{"disambiguationData":[TD([[makeQuery(id+"F0.imprint","INTERSECT",VERTEX,{"derivedFrom":[subQ0,sQuery(id+"F0.wireOp",EDGE,"E34")]}),1.0]])],"derivedFrom":subQ0})])],"isStart":false});}
            var Q32;
            {var subQ0=sQuery(id+"F0.wireOp",EDGE,"E3");Q32=makeQuery(id+"F3.opExtrude","CAP_EDGE",EDGE,{"disambiguationData":[OSD([subQ0]),TDD([makeQuery(id+"F0.imprint","IMPRINT",EDGE,{"disambiguationData":[TD([[makeQuery(id+"F0.imprint","INTERSECT",VERTEX,{"derivedFrom":[subQ0,sQuery(id+"F0.wireOp",EDGE,"E36")]}),1.0]])],"derivedFrom":subQ0})])],"isStart":false});}
            var Q33;
            {var subQ0=sQuery(id+"F0.wireOp",EDGE,"E49.MirrorCS");Q33=makeQuery(id+"F3.opExtrude","CAP_EDGE",EDGE,{"disambiguationData":[OSD([subQ0]),TDD([makeQuery(id+"F0.imprint","IMPRINT",EDGE,{"disambiguationData":[TD([[makeQuery(id+"F0.imprint","INTERSECT",VERTEX,{"derivedFrom":[subQ0,sQuery(id+"F0.wireOp",EDGE,"E82.MirrorCS")]}),1.0]])],"derivedFrom":subQ0})])],"isStart":false});}
            var Q34;
            {var subQ0=sQuery(id+"F0.wireOp",EDGE,"E49.MirrorCS");Q34=makeQuery(id+"F3.opExtrude","CAP_EDGE",EDGE,{"disambiguationData":[OSD([subQ0]),TDD([makeQuery(id+"F0.imprint","IMPRINT",EDGE,{"disambiguationData":[TD([[makeQuery(id+"F0.imprint","INTERSECT",VERTEX,{"derivedFrom":[subQ0,sQuery(id+"F0.wireOp",EDGE,"E84.MirrorCS")]}),1.0]])],"derivedFrom":subQ0})])],"isStart":false});}
            var Q35;
            {var subQ0=sQuery(id+"F0.wireOp",EDGE,"E3");Q35=makeQuery(id+"F3.opExtrude","CAP_EDGE",EDGE,{"disambiguationData":[OSD([subQ0]),TDD([makeQuery(id+"F0.imprint","IMPRINT",EDGE,{"disambiguationData":[TD([[makeQuery(id+"F0.imprint","INTERSECT",VERTEX,{"derivedFrom":[subQ0,sQuery(id+"F0.wireOp",EDGE,"E38")]}),1.0]])],"derivedFrom":subQ0})])],"isStart":false});}
            var Q36;
            {var subQ0=sQuery(id+"F0.wireOp",EDGE,"E3");Q36=makeQuery(id+"F3.opExtrude","CAP_EDGE",EDGE,{"disambiguationData":[OSD([subQ0]),TDD([makeQuery(id+"F0.imprint","IMPRINT",EDGE,{"disambiguationData":[TD([[makeQuery(id+"F0.imprint","INTERSECT",VERTEX,{"derivedFrom":[subQ0,sQuery(id+"F0.wireOp",EDGE,"E40")]}),1.0]])],"derivedFrom":subQ0})])],"isStart":false});}
            var Q37;
            {var subQ0=sQuery(id+"F0.wireOp",EDGE,"E49.MirrorCS");Q37=makeQuery(id+"F3.opExtrude","CAP_EDGE",EDGE,{"disambiguationData":[OSD([subQ0]),TDD([makeQuery(id+"F0.imprint","IMPRINT",EDGE,{"disambiguationData":[TD([[makeQuery(id+"F0.imprint","INTERSECT",VERTEX,{"derivedFrom":[subQ0,sQuery(id+"F0.wireOp",EDGE,"E86.MirrorCS")]}),1.0]])],"derivedFrom":subQ0})])],"isStart":false});}
            var Q38;
            {var subQ0=sQuery(id+"F0.wireOp",EDGE,"E49.MirrorCS");Q38=makeQuery(id+"F3.opExtrude","CAP_EDGE",EDGE,{"disambiguationData":[OSD([subQ0]),TDD([makeQuery(id+"F0.imprint","IMPRINT",EDGE,{"disambiguationData":[TD([[makeQuery(id+"F0.imprint","INTERSECT",VERTEX,{"derivedFrom":[subQ0,sQuery(id+"F0.wireOp",EDGE,"E88.MirrorCS")]}),1.0]])],"derivedFrom":subQ0})])],"isStart":false});}
            var Q39;
            {var subQ0=sQuery(id+"F0.wireOp",EDGE,"E49.MirrorCS");Q39=makeQuery(id+"F3.opExtrude","CAP_EDGE",EDGE,{"disambiguationData":[OSD([subQ0]),TDD([makeQuery(id+"F0.imprint","IMPRINT",EDGE,{"disambiguationData":[TD([[makeQuery(id+"F0.imprint","INTERSECT",VERTEX,{"derivedFrom":[subQ0,sQuery(id+"F0.wireOp",EDGE,"E90.MirrorCS")]}),1.0]])],"derivedFrom":subQ0})])],"isStart":false});}
            var Q40;
            {var subQ0=sQuery(id+"F0.wireOp",EDGE,"E49.MirrorCS");Q40=makeQuery(id+"F3.opExtrude","CAP_EDGE",EDGE,{"disambiguationData":[OSD([subQ0]),TDD([makeQuery(id+"F0.imprint","IMPRINT",EDGE,{"disambiguationData":[TD([[makeQuery(id+"F0.imprint","INTERSECT",VERTEX,{"derivedFrom":[subQ0,sQuery(id+"F0.wireOp",EDGE,"E93.MirrorCS")]}),1.0]])],"derivedFrom":subQ0})])],"isStart":false});}
            var Q41;
            {var subQ0=sQuery(id+"F0.wireOp",EDGE,"E3");Q41=makeQuery(id+"F3.opExtrude","CAP_EDGE",EDGE,{"disambiguationData":[OSD([subQ0]),TDD([makeQuery(id+"F0.imprint","IMPRINT",EDGE,{"disambiguationData":[TD([[makeQuery(id+"F0.imprint","INTERSECT",VERTEX,{"derivedFrom":[subQ0,sQuery(id+"F0.wireOp",EDGE,"E42")]}),1.0]])],"derivedFrom":subQ0})])],"isStart":false});}
            var Q42;
            {var subQ0=sQuery(id+"F0.wireOp",EDGE,"E3");Q42=makeQuery(id+"F3.opExtrude","CAP_EDGE",EDGE,{"disambiguationData":[OSD([subQ0]),TDD([makeQuery(id+"F0.imprint","IMPRINT",EDGE,{"disambiguationData":[TD([[makeQuery(id+"F0.imprint","INTERSECT",VERTEX,{"derivedFrom":[subQ0,sQuery(id+"F0.wireOp",EDGE,"E46")]}),1.0]])],"derivedFrom":subQ0})])],"isStart":false});}
            var Q43;
            {var subQ0=sQuery(id+"F0.wireOp",EDGE,"E3");Q43=makeQuery(id+"F3.opExtrude","CAP_EDGE",EDGE,{"disambiguationData":[OSD([subQ0]),TDD([makeQuery(id+"F0.imprint","IMPRINT",EDGE,{"disambiguationData":[TD([[makeQuery(id+"F0.imprint","INTERSECT",VERTEX,{"derivedFrom":[subQ0,sQuery(id+"F0.wireOp",EDGE,"E44")]}),1.0]])],"derivedFrom":subQ0})])],"isStart":false});}
            fillet(context, id + "F5", {"entities" : qUnion([Q0, Q1, Q2, Q3, Q4, Q5, Q6, Q7, Q8, Q9, Q10, Q11, Q12, Q13, Q14, Q15, Q16, Q17, Q18, Q19, Q20, Q21, Q22, Q23, Q24, Q25, Q26, Q27, Q28, Q29, Q30, Q31, Q32, Q33, Q34, Q35, Q36, Q37, Q38, Q39, Q40, Q41, Q42, Q43]), "radius" : 1 * mm, "tangentPropagation" : true, "allowEdgeOverflow" : false});
        }
    });
